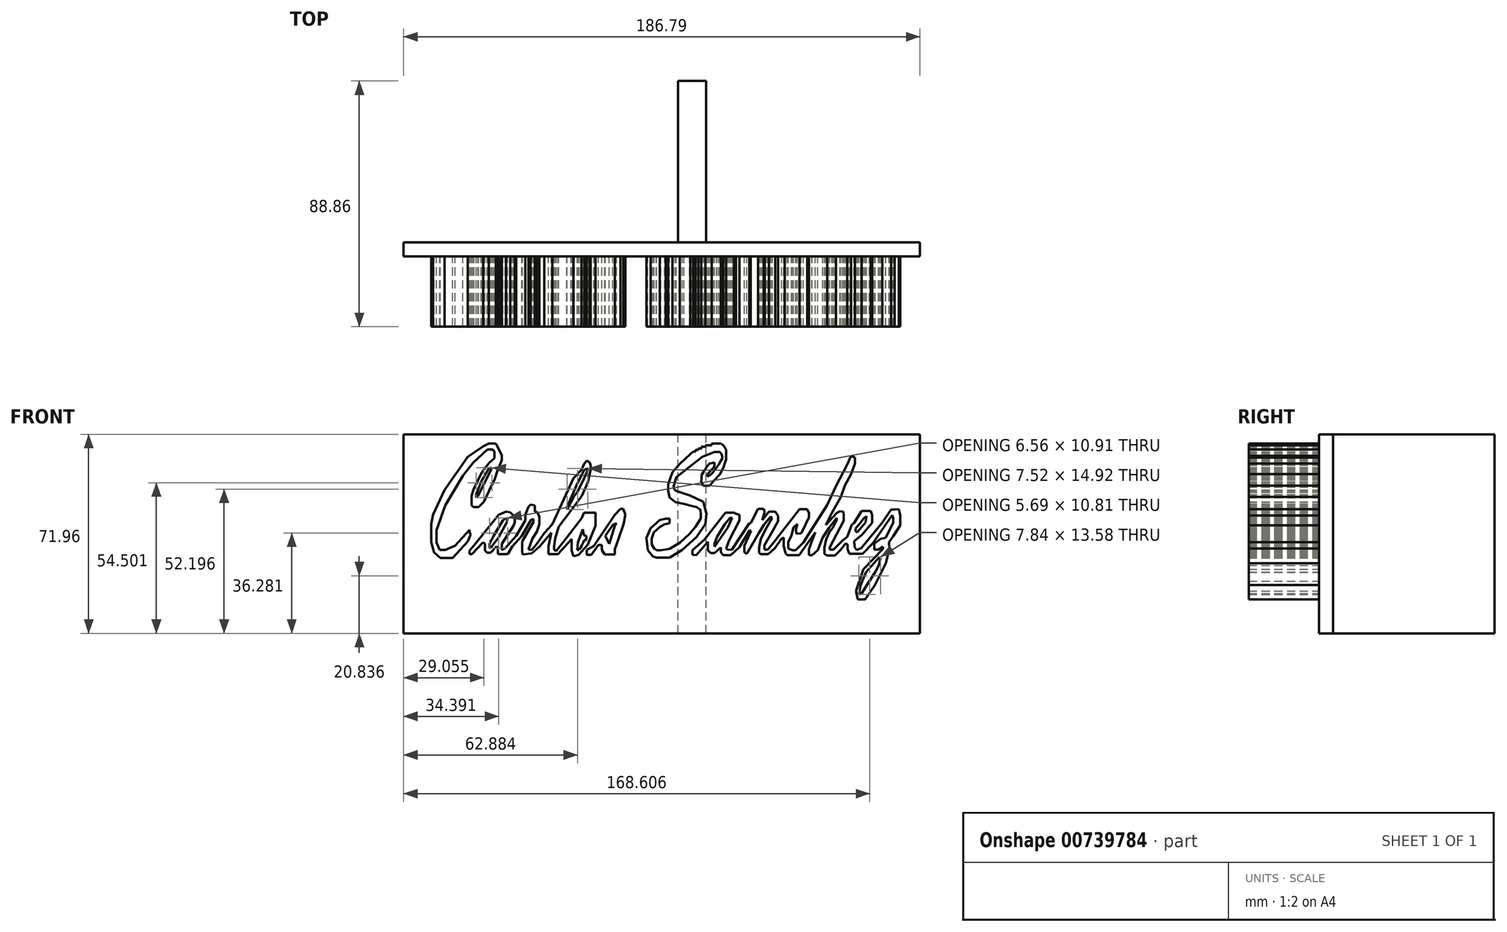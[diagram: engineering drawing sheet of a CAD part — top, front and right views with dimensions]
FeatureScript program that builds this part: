
annotation { "Feature Type Name" : "Feature", "Feature Type Description" : "" }
export const myFeature = defineFeature(function(context is Context, id is Id, definition is map)
    precondition{}
    {
        {
            var Q0;
            Q0=qCreatedBy(makeId("Front.planeOp"),FACE);
            var sketch = newSketch(context, id + "F0", { "sketchPlane" : qUnion([Q0])});
            skLineSegment(sketch, "E0", {"start": v(-63.8, 37.57) * mm, "end": v(-63.8, 39.28) * mm});
            skLineSegment(sketch, "E1", {"start": v(-68.35, 36.5) * mm, "end": v(-71.07, 33.02) * mm});
            skLineSegment(sketch, "E2", {"start": v(-71.07, 33.02) * mm, "end": v(-74.04, 26.76) * mm});
            skLineSegment(sketch, "E3", {"start": v(-74.04, 26.76) * mm, "end": v(-74.73, 24.6) * mm});
            skLineSegment(sketch, "E4", {"start": v(-74.73, 24.6) * mm, "end": v(-74.73, 21.13) * mm});
            skLineSegment(sketch, "E5", {"start": v(-74.73, 21.13) * mm, "end": v(-74.04, 20.56) * mm});
            skLineSegment(sketch, "E6", {"start": v(-74.04, 20.56) * mm, "end": v(-72.2, 20.56) * mm});
            skLineSegment(sketch, "E7", {"start": v(-72.2, 20.56) * mm, "end": v(-70.3, 22.4) * mm});
            skLineSegment(sketch, "E8", {"start": v(-70.3, 22.4) * mm, "end": v(-68.35, 26.44) * mm});
            skLineSegment(sketch, "E9", {"start": v(-68.35, 26.44) * mm, "end": v(-66.39, 30.68) * mm});
            skLineSegment(sketch, "E10", {"start": v(-66.39, 30.68) * mm, "end": v(-65.44, 33.4) * mm});
            skLineSegment(sketch, "E11", {"start": v(-65.44, 33.4) * mm, "end": v(-63.8, 37.57) * mm});
            skPoint(sketch, "E12.startSnap0", {"position": v(-63.8, 38.43) * mm});
            skLineSegment(sketch, "E13", {"start": v(-74.23, 36.5) * mm, "end": v(-75.33, 35.09) * mm});
            skLineSegment(sketch, "E14", {"start": v(-75.33, 35.09) * mm, "end": v(-77.92, 31.77) * mm});
            skLineSegment(sketch, "E15", {"start": v(-77.92, 31.77) * mm, "end": v(-84.22, 21.2) * mm});
            skLineSegment(sketch, "E16", {"start": v(-87.44, 12.09) * mm, "end": v(-87.44, 7.66) * mm});
            skLineSegment(sketch, "E17", {"start": v(-87.44, 7.66) * mm, "end": v(-86.3, 4.94) * mm});
            skLineSegment(sketch, "E18", {"start": v(-86.3, 4.94) * mm, "end": v(-84.22, 4.94) * mm});
            skLineSegment(sketch, "E19", {"start": v(-84.22, 4.94) * mm, "end": v(-80.74, 6.59) * mm});
            skLineSegment(sketch, "E20", {"start": v(-80.74, 6.59) * mm, "end": v(-76.13, 11.65) * mm});
            skLineSegment(sketch, "E21", {"start": v(-76.13, 11.65) * mm, "end": v(-75.53, 12.3) * mm});
            skLineSegment(sketch, "E22", {"start": v(-75.53, 12.3) * mm, "end": v(-75.53, 11.65) * mm});
            skLineSegment(sketch, "E23", {"start": v(-75.53, 11.65) * mm, "end": v(-75.05, 10.45) * mm});
            skLineSegment(sketch, "E24", {"start": v(-75.05, 10.45) * mm, "end": v(-76.13, 8.03) * mm});
            skLineSegment(sketch, "E25", {"start": v(-76.13, 8.03) * mm, "end": v(-78.05, 5.92) * mm});
            skLineSegment(sketch, "E26", {"start": v(-78.05, 5.92) * mm, "end": v(-81.6, 2.02) * mm});
            skLineSegment(sketch, "E27", {"start": v(-81.6, 2.02) * mm, "end": v(-86.05, 2.02) * mm});
            skLineSegment(sketch, "E28", {"start": v(-86.05, 2.02) * mm, "end": v(-88.33, 4.1) * mm});
            skLineSegment(sketch, "E29", {"start": v(-88.33, 4.1) * mm, "end": v(-89.34, 7.85) * mm});
            skLineSegment(sketch, "E30", {"start": v(-89.34, 7.85) * mm, "end": v(-89.34, 14.24) * mm});
            skLineSegment(sketch, "E31", {"start": v(-89.34, 14.24) * mm, "end": v(-88.65, 17.72) * mm});
            skLineSegment(sketch, "E32", {"start": v(-88.65, 17.72) * mm, "end": v(-84.51, 26.72) * mm});
            skLineSegment(sketch, "E33", {"start": v(-84.51, 26.72) * mm, "end": v(-76.13, 38.63) * mm});
            skLineSegment(sketch, "E34", {"start": v(-76.13, 38.63) * mm, "end": v(-70.56, 42.5) * mm});
            skLineSegment(sketch, "E35", {"start": v(-70.56, 42.5) * mm, "end": v(-68.54, 43.52) * mm});
            skLineSegment(sketch, "E36", {"start": v(-68.54, 43.52) * mm, "end": v(-65.94, 43.52) * mm});
            skLineSegment(sketch, "E37", {"start": v(-65.94, 43.52) * mm, "end": v(-65.19, 42.13) * mm});
            skLineSegment(sketch, "E38", {"start": v(-65.19, 42.13) * mm, "end": v(-64.3, 40.23) * mm});
            skLineSegment(sketch, "E39", {"start": v(-64.3, 40.23) * mm, "end": v(-63.8, 39.28) * mm});
            skLineSegment(sketch, "E40", {"start": v(-67.4, 34.6) * mm, "end": v(-72.46, 24.6) * mm});
            skLineSegment(sketch, "E41", {"start": v(-72.46, 24.6) * mm, "end": v(-73.1, 23.92) * mm});
            skLineSegment(sketch, "E42", {"start": v(-73.1, 23.92) * mm, "end": v(-73.1, 25.12) * mm});
            skLineSegment(sketch, "E43", {"start": v(-73.1, 25.12) * mm, "end": v(-71.32, 29.6) * mm});
            skLineSegment(sketch, "E44", {"start": v(-71.32, 29.6) * mm, "end": v(-68.35, 34.73) * mm});
            skLineSegment(sketch, "E45", {"start": v(-68.35, 34.73) * mm, "end": v(-67.4, 34.6) * mm});
            skLineSegment(sketch, "E46", {"start": v(-75.53, 4.75) * mm, "end": v(-73.77, 6.68) * mm});
            skLineSegment(sketch, "E47", {"start": v(-73.77, 6.68) * mm, "end": v(-64.93, 17.72) * mm});
            skLineSegment(sketch, "E48", {"start": v(-64.93, 17.72) * mm, "end": v(-62.21, 18.86) * mm});
            skLineSegment(sketch, "E49", {"start": v(-62.21, 18.86) * mm, "end": v(-60.72, 18.56) * mm});
            skLineSegment(sketch, "E50", {"start": v(-60.72, 18.56) * mm, "end": v(-59.8, 17.72) * mm});
            skLineSegment(sketch, "E51", {"start": v(-59.8, 17.72) * mm, "end": v(-59.08, 17.06) * mm});
            skLineSegment(sketch, "E52", {"start": v(-59.08, 17.06) * mm, "end": v(-59.08, 15.06) * mm});
            skLineSegment(sketch, "E53", {"start": v(-59.08, 15.06) * mm, "end": v(-59.52, 13.93) * mm});
            skLineSegment(sketch, "E54", {"start": v(-59.52, 13.93) * mm, "end": v(-63.8, 7.16) * mm});
            skLineSegment(sketch, "E55", {"start": v(-63.8, 7.16) * mm, "end": v(-63.8, 5) * mm});
            skLineSegment(sketch, "E56", {"start": v(-63.8, 5) * mm, "end": v(-62.53, 5.7) * mm});
            skLineSegment(sketch, "E57", {"start": v(-62.53, 5.7) * mm, "end": v(-58.57, 10.04) * mm});
            skLineSegment(sketch, "E58", {"start": v(-58.57, 10.04) * mm, "end": v(-55.32, 15.7) * mm});
            skLineSegment(sketch, "E59", {"start": v(-55.32, 15.7) * mm, "end": v(-55.32, 17.72) * mm});
            skLineSegment(sketch, "E60", {"start": v(-55.32, 17.72) * mm, "end": v(-54.2, 20.57) * mm});
            skLineSegment(sketch, "E61", {"start": v(-54.2, 20.57) * mm, "end": v(-53.42, 21.42) * mm});
            skLineSegment(sketch, "E62", {"start": v(-53.42, 21.42) * mm, "end": v(-51.84, 21.1) * mm});
            skLineSegment(sketch, "E63", {"start": v(-51.84, 21.1) * mm, "end": v(-51.84, 18.86) * mm});
            skLineSegment(sketch, "E64", {"start": v(-51.84, 18.86) * mm, "end": v(-51, 18.69) * mm});
            skLineSegment(sketch, "E65", {"start": v(-51, 18.69) * mm, "end": v(-50.2, 16.96) * mm});
            skLineSegment(sketch, "E66", {"start": v(-50.2, 16.96) * mm, "end": v(-50.2, 14.3) * mm});
            skLineSegment(sketch, "E67", {"start": v(-50.2, 14.3) * mm, "end": v(-51.13, 11.65) * mm});
            skLineSegment(sketch, "E68", {"start": v(-51.13, 11.65) * mm, "end": v(-52.8, 9.05) * mm});
            skLineSegment(sketch, "E69", {"start": v(-52.8, 9.05) * mm, "end": v(-53.7, 6.44) * mm});
            skLineSegment(sketch, "E70", {"start": v(-53.7, 6.44) * mm, "end": v(-54.14, 5.18) * mm});
            skLineSegment(sketch, "E71", {"start": v(-54.14, 5.18) * mm, "end": v(-53.05, 4.96) * mm});
            skLineSegment(sketch, "E72", {"start": v(-53.05, 4.96) * mm, "end": v(-51.21, 6.98) * mm});
            skLineSegment(sketch, "E73", {"start": v(-51.21, 6.98) * mm, "end": v(-48.37, 11.14) * mm});
            skLineSegment(sketch, "E74", {"start": v(-48.37, 11.14) * mm, "end": v(-45.56, 14.22) * mm});
            skLineSegment(sketch, "E75", {"start": v(-75.53, 4.25) * mm, "end": v(-75.53, 3.43) * mm});
            skLineSegment(sketch, "E76", {"start": v(-75.53, 3.43) * mm, "end": v(-74.54, 3.43) * mm});
            skLineSegment(sketch, "E77", {"start": v(-74.54, 3.43) * mm, "end": v(-70.65, 7.7) * mm});
            skLineSegment(sketch, "E78", {"start": v(-70.65, 7.7) * mm, "end": v(-69.91, 7.26) * mm});
            skLineSegment(sketch, "E79", {"start": v(-69.91, 7.26) * mm, "end": v(-69.91, 4.75) * mm});
            skLineSegment(sketch, "E80", {"start": v(-69.91, 4.75) * mm, "end": v(-69.07, 4) * mm});
            skLineSegment(sketch, "E81", {"start": v(-69.07, 4) * mm, "end": v(-67.84, 4) * mm});
            skLineSegment(sketch, "E82", {"start": v(-67.84, 4) * mm, "end": v(-65.73, 6.3) * mm});
            skLineSegment(sketch, "E83", {"start": v(-65.73, 6.3) * mm, "end": v(-65.2, 5.84) * mm});
            skLineSegment(sketch, "E84", {"start": v(-65.2, 5.84) * mm, "end": v(-65.2, 3.43) * mm});
            skLineSegment(sketch, "E85", {"start": v(-65.2, 3.43) * mm, "end": v(-61.64, 3.43) * mm});
            skLineSegment(sketch, "E86", {"start": v(-61.64, 3.43) * mm, "end": v(-59.99, 6.3) * mm});
            skLineSegment(sketch, "E87", {"start": v(-59.99, 6.3) * mm, "end": v(-56.58, 10.04) * mm});
            skLineSegment(sketch, "E88", {"start": v(-56.58, 10.04) * mm, "end": v(-53.29, 15.77) * mm});
            skLineSegment(sketch, "E89", {"start": v(-53.29, 15.77) * mm, "end": v(-52.54, 16.33) * mm});
            skLineSegment(sketch, "E90", {"start": v(-52.54, 16.33) * mm, "end": v(-52.29, 15.25) * mm});
            skLineSegment(sketch, "E91", {"start": v(-52.29, 15.25) * mm, "end": v(-56.45, 8) * mm});
            skLineSegment(sketch, "E92", {"start": v(-56.45, 8) * mm, "end": v(-56.45, 4.75) * mm});
            skLineSegment(sketch, "E93", {"start": v(-56.45, 4.75) * mm, "end": v(-56.27, 3.3) * mm});
            skLineSegment(sketch, "E94", {"start": v(-56.27, 3.3) * mm, "end": v(-52.97, 3.72) * mm});
            skLineSegment(sketch, "E95", {"start": v(-52.97, 3.72) * mm, "end": v(-50.14, 6.3) * mm});
            skLineSegment(sketch, "E96", {"start": v(-50.14, 6.3) * mm, "end": v(-45.84, 11.27) * mm});
            skLineSegment(sketch, "E97", {"start": v(-45.84, 11.27) * mm, "end": v(-46.91, 6.3) * mm});
            skLineSegment(sketch, "E98", {"start": v(-46.91, 6.3) * mm, "end": v(-46.91, 3.43) * mm});
            skLineSegment(sketch, "E99", {"start": v(-46.91, 3.43) * mm, "end": v(-43.5, 3.43) * mm});
            skLineSegment(sketch, "E100", {"start": v(-43.5, 3.43) * mm, "end": v(-41.15, 6) * mm});
            skLineSegment(sketch, "E101", {"start": v(-41.15, 6) * mm, "end": v(-38.46, 8.95) * mm});
            skLineSegment(sketch, "E102", {"start": v(-38.46, 8.95) * mm, "end": v(-38.46, 4.75) * mm});
            skLineSegment(sketch, "E103", {"start": v(-38.46, 4.75) * mm, "end": v(-37.87, 2.73) * mm});
            skLineSegment(sketch, "E104", {"start": v(-37.87, 2.73) * mm, "end": v(-36.03, 3.27) * mm});
            skLineSegment(sketch, "E105", {"start": v(-36.03, 3.27) * mm, "end": v(-32.66, 6.95) * mm});
            skLineSegment(sketch, "E106", {"start": v(-32.66, 6.95) * mm, "end": v(-29.84, 13.73) * mm});
            skLineSegment(sketch, "E107", {"start": v(-29.84, 13.73) * mm, "end": v(-29.84, 17.9) * mm});
            skLineSegment(sketch, "E108", {"start": v(-45.56, 14.22) * mm, "end": v(-37.87, 30.87) * mm});
            skLineSegment(sketch, "E109", {"start": v(-37.87, 30.87) * mm, "end": v(-35, 34.02) * mm});
            skLineSegment(sketch, "E110", {"start": v(-35, 34.02) * mm, "end": v(-33.95, 36.3) * mm});
            skLineSegment(sketch, "E111", {"start": v(-33.95, 36.3) * mm, "end": v(-33.12, 37.22) * mm});
            skLineSegment(sketch, "E112", {"start": v(-33.12, 37.22) * mm, "end": v(-32.02, 36.72) * mm});
            skLineSegment(sketch, "E113", {"start": v(-32.02, 36.72) * mm, "end": v(-31.67, 35.68) * mm});
            skLineSegment(sketch, "E114", {"start": v(-31.67, 35.68) * mm, "end": v(-31.6, 33.97) * mm});
            skLineSegment(sketch, "E115", {"start": v(-32.66, 29.42) * mm, "end": v(-33.95, 26.59) * mm});
            skLineSegment(sketch, "E116", {"start": v(-33.95, 26.59) * mm, "end": v(-34.88, 24.55) * mm});
            skLineSegment(sketch, "E117", {"start": v(-34.88, 24.55) * mm, "end": v(-38.72, 19.18) * mm});
            skLineSegment(sketch, "E118", {"start": v(-38.72, 19.18) * mm, "end": v(-43.27, 13.36) * mm});
            skLineSegment(sketch, "E119", {"start": v(-43.27, 13.36) * mm, "end": v(-44.47, 9.06) * mm});
            skLineSegment(sketch, "E120", {"start": v(-44.47, 9.06) * mm, "end": v(-44.85, 6.28) * mm});
            skLineSegment(sketch, "E121", {"start": v(-44.85, 6.28) * mm, "end": v(-44.85, 5.01) * mm});
            skLineSegment(sketch, "E122", {"start": v(-44.85, 5.01) * mm, "end": v(-44.1, 4.66) * mm});
            skLineSegment(sketch, "E123", {"start": v(-44.1, 4.66) * mm, "end": v(-40.24, 9.5) * mm});
            skLineSegment(sketch, "E124", {"start": v(-40.24, 9.5) * mm, "end": v(-34.88, 16.58) * mm});
            skLineSegment(sketch, "E125", {"start": v(-34.88, 16.58) * mm, "end": v(-34.02, 18.46) * mm});
            skLineSegment(sketch, "E126", {"start": v(-34.02, 18.46) * mm, "end": v(-31.95, 18.46) * mm});
            skLineSegment(sketch, "E127", {"start": v(-31.95, 18.46) * mm, "end": v(-29.87, 18.46) * mm});
            skLineSegment(sketch, "E128", {"start": v(-29.87, 18.46) * mm, "end": v(-29.84, 17.9) * mm});
            skLineSegment(sketch, "E129", {"start": v(-31, 16.96) * mm, "end": v(-32.04, 15.59) * mm});
            skLineSegment(sketch, "E130", {"start": v(-32.66, 29.42) * mm, "end": v(-31.6, 33.97) * mm});
            skLineSegment(sketch, "E131", {"start": v(-32.66, 33.97) * mm, "end": v(-33.97, 31.09) * mm});
            skLineSegment(sketch, "E132", {"start": v(-40.17, 19.55) * mm, "end": v(-37.45, 24.68) * mm});
            skLineSegment(sketch, "E133", {"start": v(-37.45, 24.68) * mm, "end": v(-36.5, 25.81) * mm});
            skLineSegment(sketch, "E134", {"start": v(-36.5, 25.81) * mm, "end": v(-33.97, 31.09) * mm});
            skLineSegment(sketch, "E135", {"start": v(-40.17, 19.55) * mm, "end": v(-40.17, 20.44) * mm});
            skLineSegment(sketch, "E136", {"start": v(-40.17, 20.44) * mm, "end": v(-36.5, 29.04) * mm});
            skLineSegment(sketch, "E137", {"start": v(-36.5, 29.04) * mm, "end": v(-33.89, 33.97) * mm});
            skLineSegment(sketch, "E138", {"start": v(-33.89, 33.97) * mm, "end": v(-32.66, 34.48) * mm});
            skLineSegment(sketch, "E139", {"start": v(-33.03, 4.95) * mm, "end": v(-30.56, 6.34) * mm});
            skLineSegment(sketch, "E140", {"start": v(-30.56, 6.34) * mm, "end": v(-26.83, 11.84) * mm});
            skLineSegment(sketch, "E141", {"start": v(-26.83, 11.84) * mm, "end": v(-22.85, 17.66) * mm});
            skLineSegment(sketch, "E142", {"start": v(-22.85, 17.66) * mm, "end": v(-20.82, 19.88) * mm});
            skLineSegment(sketch, "E143", {"start": v(-20.82, 19.88) * mm, "end": v(-19.81, 19.88) * mm});
            skLineSegment(sketch, "E144", {"start": v(-19.81, 19.88) * mm, "end": v(-19.05, 17.66) * mm});
            skLineSegment(sketch, "E145", {"start": v(-19.05, 17.66) * mm, "end": v(-19.75, 14.43) * mm});
            skLineSegment(sketch, "E146", {"start": v(-19.75, 14.43) * mm, "end": v(-21.65, 8.8) * mm});
            skLineSegment(sketch, "E147", {"start": v(-21.65, 8.8) * mm, "end": v(-22.85, 5.26) * mm});
            skLineSegment(sketch, "E148", {"start": v(-24.87, 7.22) * mm, "end": v(-22.85, 13.8) * mm});
            skLineSegment(sketch, "E149", {"start": v(-22.85, 13.8) * mm, "end": v(-22.2, 14.7) * mm});
            skLineSegment(sketch, "E150", {"start": v(-22.2, 14.7) * mm, "end": v(-23.6, 13.99) * mm});
            skLineSegment(sketch, "E151", {"start": v(-23.6, 13.99) * mm, "end": v(-26.38, 10.14) * mm});
            skLineSegment(sketch, "E152", {"start": v(-26.38, 10.14) * mm, "end": v(-24.87, 7.22) * mm});
            skLineSegment(sketch, "E153", {"start": v(-33.03, 4.95) * mm, "end": v(-33.03, 3.24) * mm});
            skLineSegment(sketch, "E154", {"start": v(-33.03, 3.24) * mm, "end": v(-31.38, 3.24) * mm});
            skLineSegment(sketch, "E155", {"start": v(-31.38, 3.24) * mm, "end": v(-28.85, 6.77) * mm});
            skLineSegment(sketch, "E156", {"start": v(-28.85, 6.77) * mm, "end": v(-27.65, 6.77) * mm});
            skLineSegment(sketch, "E157", {"start": v(-27.65, 6.77) * mm, "end": v(-27.65, 4.95) * mm});
            skLineSegment(sketch, "E158", {"start": v(-27.65, 4.95) * mm, "end": v(-26.64, 3.37) * mm});
            skLineSegment(sketch, "E159", {"start": v(-26.64, 3.37) * mm, "end": v(-22.85, 3.37) * mm});
            skLineSegment(sketch, "E160", {"start": v(-22.85, 3.37) * mm, "end": v(-22.85, 5.26) * mm});
            skLineSegment(sketch, "E161", {"start": v(-9.13, 2.67) * mm, "end": v(-7.93, 2.27) * mm});
            skLineSegment(sketch, "E162", {"start": v(-7.93, 2.27) * mm, "end": v(-3.06, 2.27) * mm});
            skLineSegment(sketch, "E163", {"start": v(-3.06, 2.27) * mm, "end": v(1.43, 4.95) * mm});
            skLineSegment(sketch, "E164", {"start": v(1.43, 4.95) * mm, "end": v(6.75, 9.7) * mm});
            skLineSegment(sketch, "E165", {"start": v(9.09, 22.46) * mm, "end": v(4.34, 24.68) * mm});
            skLineSegment(sketch, "E166", {"start": v(4.34, 24.68) * mm, "end": v(-1.06, 26.5) * mm});
            skLineSegment(sketch, "E167", {"start": v(-3.53, 28.7) * mm, "end": v(-3.53, 26.32) * mm});
            skLineSegment(sketch, "E168", {"start": v(-3.53, 26.32) * mm, "end": v(-3.06, 23.92) * mm});
            skLineSegment(sketch, "E169", {"start": v(-3.06, 23.92) * mm, "end": v(-0.9, 22.34) * mm});
            skLineSegment(sketch, "E170", {"start": v(-0.9, 22.34) * mm, "end": v(2.07, 21.64) * mm});
            skLineSegment(sketch, "E171", {"start": v(2.07, 21.64) * mm, "end": v(5.1, 20.82) * mm});
            skLineSegment(sketch, "E172", {"start": v(5.1, 20.82) * mm, "end": v(6.75, 20.44) * mm});
            skLineSegment(sketch, "E173", {"start": v(6.75, 20.44) * mm, "end": v(8.07, 19.5) * mm});
            skLineSegment(sketch, "E174", {"start": v(8.2, 17.66) * mm, "end": v(8.2, 16.4) * mm});
            skLineSegment(sketch, "E175", {"start": v(8.2, 16.4) * mm, "end": v(6.37, 13.36) * mm});
            skLineSegment(sketch, "E176", {"start": v(6.37, 13.36) * mm, "end": v(4.22, 10.83) * mm});
            skLineSegment(sketch, "E177", {"start": v(0.68, 7.73) * mm, "end": v(-3.06, 5.4) * mm});
            skLineSegment(sketch, "E178", {"start": v(-3.06, 5.4) * mm, "end": v(-6.28, 4.88) * mm});
            skLineSegment(sketch, "E179", {"start": v(-6.28, 4.88) * mm, "end": v(-7.73, 4.88) * mm});
            skLineSegment(sketch, "E180", {"start": v(5.23, 4.88) * mm, "end": v(9.5, 8.7) * mm});
            skLineSegment(sketch, "E181", {"start": v(9.5, 8.7) * mm, "end": v(17.12, 18.42) * mm});
            skLineSegment(sketch, "E182", {"start": v(17.12, 18.42) * mm, "end": v(20.15, 18.42) * mm});
            skLineSegment(sketch, "E183", {"start": v(20.15, 18.42) * mm, "end": v(20.91, 18.04) * mm});
            skLineSegment(sketch, "E184", {"start": v(20.91, 18.04) * mm, "end": v(22.19, 17.76) * mm});
            skLineSegment(sketch, "E185", {"start": v(5.23, 4.88) * mm, "end": v(5.23, 3.18) * mm});
            skLineSegment(sketch, "E186", {"start": v(5.23, 3.18) * mm, "end": v(6.56, 3.11) * mm});
            skLineSegment(sketch, "E187", {"start": v(6.56, 3.11) * mm, "end": v(10.8, 7.92) * mm});
            skLineSegment(sketch, "E188", {"start": v(10.8, 7.92) * mm, "end": v(10.8, 4.88) * mm});
            skLineSegment(sketch, "E189", {"start": v(10.8, 4.88) * mm, "end": v(11.74, 3.82) * mm});
            skLineSegment(sketch, "E190", {"start": v(11.74, 3.82) * mm, "end": v(13.2, 3.87) * mm});
            skLineSegment(sketch, "E191", {"start": v(13.2, 3.87) * mm, "end": v(15.42, 5.86) * mm});
            skLineSegment(sketch, "E192", {"start": v(15.42, 5.86) * mm, "end": v(15.42, 4.13) * mm});
            skLineSegment(sketch, "E193", {"start": v(15.42, 4.13) * mm, "end": v(16.32, 3.11) * mm});
            skLineSegment(sketch, "E194", {"start": v(16.32, 3.11) * mm, "end": v(19.01, 3.11) * mm});
            skLineSegment(sketch, "E195", {"start": v(19.01, 3.11) * mm, "end": v(22.25, 6) * mm});
            skLineSegment(sketch, "E196", {"start": v(22.25, 6) * mm, "end": v(25.84, 12.16) * mm});
            skLineSegment(sketch, "E197", {"start": v(25.84, 12.16) * mm, "end": v(26.32, 11.88) * mm});
            skLineSegment(sketch, "E198", {"start": v(26.32, 11.88) * mm, "end": v(25.2, 9.37) * mm});
            skLineSegment(sketch, "E199", {"start": v(25.2, 9.37) * mm, "end": v(23.95, 6.6) * mm});
            skLineSegment(sketch, "E200", {"start": v(23.95, 6.6) * mm, "end": v(23.95, 4.06) * mm});
            skLineSegment(sketch, "E201", {"start": v(23.95, 4.06) * mm, "end": v(24.83, 3.62) * mm});
            skLineSegment(sketch, "E202", {"start": v(24.83, 3.62) * mm, "end": v(29.13, 11.14) * mm});
            skLineSegment(sketch, "E203", {"start": v(29.13, 11.14) * mm, "end": v(31.1, 14.18) * mm});
            skLineSegment(sketch, "E204", {"start": v(31.1, 14.18) * mm, "end": v(33.43, 17.09) * mm});
            skLineSegment(sketch, "E205", {"start": v(33.43, 17.09) * mm, "end": v(34.04, 16.6) * mm});
            skLineSegment(sketch, "E206", {"start": v(34.04, 16.6) * mm, "end": v(31.91, 12.98) * mm});
            skLineSegment(sketch, "E207", {"start": v(31.91, 12.98) * mm, "end": v(29.89, 9.12) * mm});
            skLineSegment(sketch, "E208", {"start": v(29.89, 9.12) * mm, "end": v(29.32, 5.9) * mm});
            skLineSegment(sketch, "E209", {"start": v(29.32, 5.9) * mm, "end": v(29.32, 3.94) * mm});
            skLineSegment(sketch, "E210", {"start": v(29.32, 3.94) * mm, "end": v(29.76, 3.43) * mm});
            skLineSegment(sketch, "E211", {"start": v(29.76, 3.43) * mm, "end": v(32.55, 3.43) * mm});
            skLineSegment(sketch, "E212", {"start": v(32.55, 3.43) * mm, "end": v(35, 5.62) * mm});
            skLineSegment(sketch, "E213", {"start": v(35, 5.62) * mm, "end": v(37.48, 9.12) * mm});
            skLineSegment(sketch, "E214", {"start": v(37.48, 9.12) * mm, "end": v(38.24, 9.5) * mm});
            skLineSegment(sketch, "E215", {"start": v(38.24, 9.5) * mm, "end": v(38.24, 6.6) * mm});
            skLineSegment(sketch, "E216", {"start": v(38.24, 6.6) * mm, "end": v(38.87, 3.8) * mm});
            skLineSegment(sketch, "E217", {"start": v(38.87, 3.8) * mm, "end": v(39.49, 3.11) * mm});
            skLineSegment(sketch, "E218", {"start": v(39.49, 3.11) * mm, "end": v(43.8, 3.11) * mm});
            skLineSegment(sketch, "E219", {"start": v(43.8, 3.11) * mm, "end": v(48.3, 9.63) * mm});
            skLineSegment(sketch, "E220", {"start": v(48.3, 9.63) * mm, "end": v(49.68, 11.33) * mm});
            skLineSegment(sketch, "E221", {"start": v(49.68, 11.33) * mm, "end": v(48.42, 8.49) * mm});
            skLineSegment(sketch, "E222", {"start": v(48.42, 8.49) * mm, "end": v(47.28, 5.2) * mm});
            skLineSegment(sketch, "E223", {"start": v(47.28, 5.2) * mm, "end": v(47.28, 3.11) * mm});
            skLineSegment(sketch, "E224", {"start": v(47.28, 3.11) * mm, "end": v(48.48, 3.11) * mm});
            skLineSegment(sketch, "E225", {"start": v(48.48, 3.11) * mm, "end": v(50.46, 4.88) * mm});
            skLineSegment(sketch, "E226", {"start": v(50.46, 4.88) * mm, "end": v(52.27, 9.5) * mm});
            skLineSegment(sketch, "E227", {"start": v(52.27, 9.5) * mm, "end": v(54.74, 13.1) * mm});
            skLineSegment(sketch, "E228", {"start": v(54.74, 13.1) * mm, "end": v(57.4, 16.58) * mm});
            skLineSegment(sketch, "E229", {"start": v(57.4, 16.58) * mm, "end": v(57.4, 15.76) * mm});
            skLineSegment(sketch, "E230", {"start": v(57.4, 15.76) * mm, "end": v(55.94, 13.04) * mm});
            skLineSegment(sketch, "E231", {"start": v(55.94, 13.04) * mm, "end": v(54.81, 11.56) * mm});
            skLineSegment(sketch, "E232", {"start": v(54.81, 11.56) * mm, "end": v(53.54, 8.87) * mm});
            skLineSegment(sketch, "E233", {"start": v(53.54, 8.87) * mm, "end": v(52.97, 5.9) * mm});
            skLineSegment(sketch, "E234", {"start": v(52.97, 5.9) * mm, "end": v(52.97, 3.62) * mm});
            skLineSegment(sketch, "E235", {"start": v(52.97, 3.62) * mm, "end": v(53.81, 2.98) * mm});
            skLineSegment(sketch, "E236", {"start": v(53.81, 2.98) * mm, "end": v(56.7, 2.98) * mm});
            skLineSegment(sketch, "E237", {"start": v(56.7, 2.98) * mm, "end": v(58.79, 4.95) * mm});
            skLineSegment(sketch, "E238", {"start": v(58.79, 4.95) * mm, "end": v(60.66, 7.4) * mm});
            skLineSegment(sketch, "E239", {"start": v(22.19, 17.76) * mm, "end": v(22.19, 15.63) * mm});
            skPoint(sketch, "E239.endSnap0", {"position": v(32.26, 15.63) * mm});
            skLineSegment(sketch, "E240", {"start": v(22.19, 15.63) * mm, "end": v(20.66, 12.72) * mm});
            skLineSegment(sketch, "E241", {"start": v(20.66, 12.72) * mm, "end": v(18.38, 8.37) * mm});
            skLineSegment(sketch, "E242", {"start": v(18.38, 8.37) * mm, "end": v(17.3, 5.33) * mm});
            skLineSegment(sketch, "E243", {"start": v(17.3, 5.33) * mm, "end": v(17.8, 5.15) * mm});
            skLineSegment(sketch, "E244", {"start": v(17.8, 5.15) * mm, "end": v(19.46, 5.01) * mm});
            skLineSegment(sketch, "E245", {"start": v(19.46, 5.01) * mm, "end": v(25.78, 14.62) * mm});
            skLineSegment(sketch, "E246", {"start": v(25.78, 14.62) * mm, "end": v(26.22, 14.62) * mm});
            skLineSegment(sketch, "E247", {"start": v(26.22, 14.62) * mm, "end": v(28.98, 19.88) * mm});
            skLineSegment(sketch, "E248", {"start": v(28.98, 19.88) * mm, "end": v(30.96, 19.88) * mm});
            skLineSegment(sketch, "E249", {"start": v(30.96, 19.88) * mm, "end": v(31.34, 18.67) * mm});
            skLineSegment(sketch, "E250", {"start": v(31.34, 18.67) * mm, "end": v(30.46, 15.76) * mm});
            skLineSegment(sketch, "E251", {"start": v(30.46, 15.76) * mm, "end": v(32.92, 18.82) * mm});
            skLineSegment(sketch, "E252", {"start": v(32.92, 18.82) * mm, "end": v(35.14, 18.82) * mm});
            skLineSegment(sketch, "E253", {"start": v(35.14, 18.82) * mm, "end": v(36.21, 17.34) * mm});
            skLineSegment(sketch, "E254", {"start": v(36.21, 17.34) * mm, "end": v(36.21, 15.38) * mm});
            skLineSegment(sketch, "E255", {"start": v(36.21, 15.38) * mm, "end": v(34.06, 11.71) * mm});
            skLineSegment(sketch, "E256", {"start": v(34.06, 11.71) * mm, "end": v(31.22, 6.72) * mm});
            skLineSegment(sketch, "E257", {"start": v(31.22, 6.72) * mm, "end": v(31.22, 5.07) * mm});
            skLineSegment(sketch, "E258", {"start": v(31.22, 5.07) * mm, "end": v(32.42, 5.07) * mm});
            skLineSegment(sketch, "E259", {"start": v(32.42, 5.07) * mm, "end": v(35.14, 8.49) * mm});
            skLineSegment(sketch, "E260", {"start": v(35.14, 8.49) * mm, "end": v(38.62, 12.92) * mm});
            skLineSegment(sketch, "E261", {"start": v(38.62, 12.92) * mm, "end": v(43.86, 19.74) * mm});
            skLineSegment(sketch, "E262", {"start": v(43.86, 19.74) * mm, "end": v(46.65, 19.74) * mm});
            skLineSegment(sketch, "E263", {"start": v(46.65, 19.74) * mm, "end": v(47.28, 18.35) * mm});
            skLineSegment(sketch, "E264", {"start": v(47.28, 18.35) * mm, "end": v(47.28, 16.77) * mm});
            skLineSegment(sketch, "E265", {"start": v(47.28, 16.77) * mm, "end": v(46.14, 14.37) * mm});
            skLineSegment(sketch, "E266", {"start": v(46.14, 14.37) * mm, "end": v(44.5, 10.95) * mm});
            skLineSegment(sketch, "E267", {"start": v(44.5, 10.95) * mm, "end": v(42.73, 10.83) * mm});
            skLineSegment(sketch, "E268", {"start": v(42.73, 10.83) * mm, "end": v(42.6, 12.5) * mm});
            skLineSegment(sketch, "E269", {"start": v(42.6, 12.5) * mm, "end": v(43.17, 14.43) * mm});
            skLineSegment(sketch, "E270", {"start": v(43.17, 14.43) * mm, "end": v(41.71, 13.17) * mm});
            skLineSegment(sketch, "E271", {"start": v(41.71, 13.17) * mm, "end": v(40.96, 10.2) * mm});
            skLineSegment(sketch, "E272", {"start": v(40.96, 10.2) * mm, "end": v(39.82, 7.86) * mm});
            skLineSegment(sketch, "E273", {"start": v(39.82, 7.86) * mm, "end": v(39.82, 5.45) * mm});
            skLineSegment(sketch, "E274", {"start": v(39.82, 5.45) * mm, "end": v(41.4, 4.88) * mm});
            skLineSegment(sketch, "E275", {"start": v(41.4, 4.88) * mm, "end": v(42.47, 4.88) * mm});
            skLineSegment(sketch, "E276", {"start": v(42.47, 4.88) * mm, "end": v(45.25, 7.73) * mm});
            skLineSegment(sketch, "E277", {"start": v(45.25, 7.73) * mm, "end": v(48.54, 12.85) * mm});
            skLineSegment(sketch, "E278", {"start": v(48.54, 12.85) * mm, "end": v(53.98, 21.2) * mm});
            skLineSegment(sketch, "E279", {"start": v(53.98, 21.2) * mm, "end": v(57.14, 28.1) * mm});
            skLineSegment(sketch, "E280", {"start": v(57.14, 28.1) * mm, "end": v(61.19, 35.87) * mm});
            skLineSegment(sketch, "E281", {"start": v(61.19, 35.87) * mm, "end": v(62.52, 39.03) * mm});
            skLineSegment(sketch, "E282", {"start": v(62.52, 39.03) * mm, "end": v(64, 38.4) * mm});
            skLineSegment(sketch, "E283", {"start": v(64, 38.4) * mm, "end": v(64, 36.18) * mm});
            skLineSegment(sketch, "E284", {"start": v(64, 36.18) * mm, "end": v(62.52, 32.4) * mm});
            skLineSegment(sketch, "E285", {"start": v(62.52, 32.4) * mm, "end": v(60.3, 28.28) * mm});
            skLineSegment(sketch, "E286", {"start": v(60.3, 28.28) * mm, "end": v(58.85, 24.23) * mm});
            skLineSegment(sketch, "E287", {"start": v(58.85, 24.23) * mm, "end": v(55.56, 18.29) * mm});
            skLineSegment(sketch, "E288", {"start": v(55.56, 18.29) * mm, "end": v(53.41, 13.99) * mm});
            skLineSegment(sketch, "E289", {"start": v(53.41, 13.99) * mm, "end": v(57.4, 18.29) * mm});
            skLineSegment(sketch, "E290", {"start": v(57.4, 18.29) * mm, "end": v(58.53, 18.99) * mm});
            skLineSegment(sketch, "E291", {"start": v(58.53, 18.99) * mm, "end": v(59.74, 18.86) * mm});
            skLineSegment(sketch, "E292", {"start": v(59.74, 18.86) * mm, "end": v(59.92, 17.6) * mm});
            skLineSegment(sketch, "E293", {"start": v(59.92, 17.6) * mm, "end": v(59.92, 15.57) * mm});
            skLineSegment(sketch, "E294", {"start": v(59.92, 15.57) * mm, "end": v(54.87, 5.9) * mm});
            skLineSegment(sketch, "E295", {"start": v(54.87, 5.9) * mm, "end": v(54.87, 5.07) * mm});
            skLineSegment(sketch, "E296", {"start": v(54.87, 5.07) * mm, "end": v(56.26, 5.07) * mm});
            skLineSegment(sketch, "E297", {"start": v(56.26, 5.07) * mm, "end": v(59.55, 8.43) * mm});
            skLineSegment(sketch, "E298", {"start": v(59.55, 8.43) * mm, "end": v(61.13, 9.75) * mm});
            skLineSegment(sketch, "E299", {"start": v(61.13, 9.75) * mm, "end": v(62.83, 14.18) * mm});
            skLineSegment(sketch, "E300", {"start": v(62.83, 14.18) * mm, "end": v(63.53, 14.69) * mm});
            skLineSegment(sketch, "E301", {"start": v(63.53, 14.69) * mm, "end": v(66.38, 19.06) * mm});
            skLineSegment(sketch, "E302", {"start": v(66.38, 19.06) * mm, "end": v(67.96, 19.06) * mm});
            skLineSegment(sketch, "E303", {"start": v(67.96, 19.06) * mm, "end": v(69.73, 19.06) * mm});
            skLineSegment(sketch, "E304", {"start": v(60.66, 7.4) * mm, "end": v(61.28, 6.93) * mm});
            skLineSegment(sketch, "E305", {"start": v(61.28, 6.93) * mm, "end": v(61.25, 5.2) * mm});
            skLineSegment(sketch, "E306", {"start": v(61.25, 5.2) * mm, "end": v(61.95, 3.56) * mm});
            skLineSegment(sketch, "E307", {"start": v(61.95, 3.56) * mm, "end": v(64.1, 3.56) * mm});
            skLineSegment(sketch, "E308", {"start": v(64.1, 3.56) * mm, "end": v(66.75, 3.56) * mm});
            skLineSegment(sketch, "E309", {"start": v(66.75, 3.56) * mm, "end": v(70.48, 7.4) * mm});
            skLineSegment(sketch, "E310", {"start": v(70.48, 7.4) * mm, "end": v(77.44, 17.53) * mm});
            skLineSegment(sketch, "E311", {"start": v(69.73, 19.06) * mm, "end": v(70.23, 17.6) * mm});
            skLineSegment(sketch, "E312", {"start": v(70.23, 17.6) * mm, "end": v(70.23, 14.75) * mm});
            skLineSegment(sketch, "E313", {"start": v(70.23, 14.75) * mm, "end": v(66.56, 10.45) * mm});
            skLineSegment(sketch, "E314", {"start": v(66.56, 10.45) * mm, "end": v(63.72, 8.17) * mm});
            skLineSegment(sketch, "E315", {"start": v(63.72, 8.17) * mm, "end": v(63.78, 5.96) * mm});
            skLineSegment(sketch, "E316", {"start": v(63.78, 5.96) * mm, "end": v(64.67, 4.95) * mm});
            skLineSegment(sketch, "E317", {"start": v(64.67, 4.95) * mm, "end": v(66.31, 5.64) * mm});
            skLineSegment(sketch, "E318", {"start": v(66.31, 5.64) * mm, "end": v(73.84, 14.94) * mm});
            skLineSegment(sketch, "E319", {"start": v(73.84, 14.94) * mm, "end": v(77.02, 19.58) * mm});
            skLineSegment(sketch, "E320", {"start": v(77.02, 19.58) * mm, "end": v(78.33, 19.58) * mm});
            skLineSegment(sketch, "E321", {"start": v(78.33, 19.58) * mm, "end": v(79.9, 19.68) * mm});
            skLineSegment(sketch, "E322", {"start": v(79.9, 19.68) * mm, "end": v(80.41, 17.47) * mm});
            skLineSegment(sketch, "E323", {"start": v(80.41, 17.47) * mm, "end": v(80.41, 13.86) * mm});
            skLineSegment(sketch, "E324", {"start": v(80.41, 13.86) * mm, "end": v(77.82, 10) * mm});
            skLineSegment(sketch, "E325", {"start": v(77.82, 10) * mm, "end": v(76.34, 7.85) * mm});
            skLineSegment(sketch, "E326", {"start": v(76.34, 7.85) * mm, "end": v(76.4, 5.45) * mm});
            skLineSegment(sketch, "E327", {"start": v(76.4, 5.45) * mm, "end": v(75.16, 0.2) * mm});
            skLineSegment(sketch, "E328", {"start": v(75.16, 0.2) * mm, "end": v(71.18, -7.64) * mm});
            skLineSegment(sketch, "E329", {"start": v(71.18, -7.64) * mm, "end": v(68.7, -11.32) * mm});
            skLineSegment(sketch, "E330", {"start": v(68.7, -11.32) * mm, "end": v(67.65, -12.9) * mm});
            skLineSegment(sketch, "E331", {"start": v(67.65, -12.9) * mm, "end": v(65.05, -12.9) * mm});
            skLineSegment(sketch, "E332", {"start": v(65.05, -12.9) * mm, "end": v(64.35, -9.91) * mm});
            skLineSegment(sketch, "E333", {"start": v(64.35, -9.91) * mm, "end": v(67.07, -1.94) * mm});
            skLineSegment(sketch, "E334", {"start": v(67.07, -1.94) * mm, "end": v(74.15, 5.33) * mm});
            skLineSegment(sketch, "E335", {"start": v(74.15, 5.33) * mm, "end": v(74.15, 6.15) * mm});
            skLineSegment(sketch, "E336", {"start": v(74.15, 6.15) * mm, "end": v(72.5, 5.14) * mm});
            skLineSegment(sketch, "E337", {"start": v(72.5, 5.14) * mm, "end": v(70.93, 5.14) * mm});
            skLineSegment(sketch, "E338", {"start": v(70.93, 5.14) * mm, "end": v(70.93, 7.35) * mm});
            skLineSegment(sketch, "E339", {"start": v(70.93, 7.35) * mm, "end": v(73.4, 9.12) * mm});
            skLineSegment(sketch, "E340", {"start": v(73.4, 9.12) * mm, "end": v(75.04, 9.37) * mm});
            skLineSegment(sketch, "E341", {"start": v(75.04, 9.37) * mm, "end": v(77.77, 14.84) * mm});
            skLineSegment(sketch, "E342", {"start": v(77.77, 14.84) * mm, "end": v(77.77, 16.46) * mm});
            skLineSegment(sketch, "E343", {"start": v(77.77, 16.46) * mm, "end": v(77.44, 17.53) * mm});
            skLineSegment(sketch, "E344", {"start": v(13.2, 6.15) * mm, "end": v(17.94, 13.1) * mm});
            skLineSegment(sketch, "E345", {"start": v(17.94, 13.1) * mm, "end": v(19.52, 16.52) * mm});
            skLineSegment(sketch, "E346", {"start": v(19.52, 16.52) * mm, "end": v(18.89, 16.7) * mm});
            skLineSegment(sketch, "E347", {"start": v(18.89, 16.7) * mm, "end": v(16.8, 14.3) * mm});
            skLineSegment(sketch, "E348", {"start": v(16.8, 14.3) * mm, "end": v(14.02, 9.7) * mm});
            skLineSegment(sketch, "E349", {"start": v(14.02, 9.7) * mm, "end": v(13.2, 7.28) * mm});
            skLineSegment(sketch, "E350", {"start": v(13.2, 7.28) * mm, "end": v(13.2, 6.15) * mm});
            skLineSegment(sketch, "E351", {"start": v(-87.44, 12.09) * mm, "end": v(-84.22, 21.2) * mm});
            skLineSegment(sketch, "E352", {"start": v(-75.53, 4.25) * mm, "end": v(-75.53, 4.75) * mm});
            skLineSegment(sketch, "E353", {"start": v(-67.83, 5.65) * mm, "end": v(-64.99, 9.61) * mm});
            skLineSegment(sketch, "E354", {"start": v(-64.99, 9.61) * mm, "end": v(-61.98, 14.85) * mm});
            skLineSegment(sketch, "E355", {"start": v(-61.98, 14.85) * mm, "end": v(-61.63, 16.43) * mm});
            skLineSegment(sketch, "E356", {"start": v(-61.63, 16.43) * mm, "end": v(-62.18, 16.56) * mm});
            skLineSegment(sketch, "E357", {"start": v(-62.18, 16.56) * mm, "end": v(-63.36, 15.67) * mm});
            skLineSegment(sketch, "E358", {"start": v(-63.36, 15.67) * mm, "end": v(-65.34, 12.51) * mm});
            skLineSegment(sketch, "E359", {"start": v(-65.34, 12.51) * mm, "end": v(-66.82, 9.92) * mm});
            skLineSegment(sketch, "E360", {"start": v(-66.82, 9.92) * mm, "end": v(-68.2, 7.12) * mm});
            skLineSegment(sketch, "E361", {"start": v(-68.2, 7.12) * mm, "end": v(-68.2, 5.8) * mm});
            skLineSegment(sketch, "E362", {"start": v(-68.2, 5.8) * mm, "end": v(-67.83, 5.65) * mm});
            skLineSegment(sketch, "E363", {"start": v(-74.23, 36.5) * mm, "end": v(-68.95, 41.28) * mm});
            skLineSegment(sketch, "E364", {"start": v(-68.95, 41.28) * mm, "end": v(-66.97, 41.28) * mm});
            skLineSegment(sketch, "E365", {"start": v(-66.97, 41.28) * mm, "end": v(-66.46, 40.46) * mm});
            skLineSegment(sketch, "E366", {"start": v(-66.46, 40.46) * mm, "end": v(-66.46, 38.2) * mm});
            skLineSegment(sketch, "E367", {"start": v(-66.46, 38.2) * mm, "end": v(-68.35, 36.5) * mm});
            skLineSegment(sketch, "E368", {"start": v(0.68, 7.73) * mm, "end": v(4.22, 10.83) * mm});
            skLineSegment(sketch, "E369", {"start": v(6.75, 9.7) * mm, "end": v(9.9, 14.35) * mm});
            skLineSegment(sketch, "E370", {"start": v(-9.13, 2.67) * mm, "end": v(-10.98, 4.88) * mm});
            skPoint(sketch, "E370.endSnap0", {"position": v(-7, 4.88) * mm});
            skLineSegment(sketch, "E371", {"start": v(-10.98, 4.88) * mm, "end": v(-11.52, 9.3) * mm});
            skLineSegment(sketch, "E372", {"start": v(-11.52, 9.3) * mm, "end": v(-9.97, 12.87) * mm});
            skLineSegment(sketch, "E373", {"start": v(-9.97, 12.87) * mm, "end": v(-6.66, 15.78) * mm});
            skLineSegment(sketch, "E374", {"start": v(-6.66, 15.78) * mm, "end": v(-4.5, 16.36) * mm});
            skLineSegment(sketch, "E375", {"start": v(-4.5, 16.36) * mm, "end": v(-3.1, 16.36) * mm});
            skLineSegment(sketch, "E376", {"start": v(-3.1, 16.36) * mm, "end": v(-3.1, 14.7) * mm});
            skLineSegment(sketch, "E377", {"start": v(-3.1, 14.7) * mm, "end": v(-4.9, 14.27) * mm});
            skLineSegment(sketch, "E378", {"start": v(-4.9, 14.27) * mm, "end": v(-6.56, 13.44) * mm});
            skLineSegment(sketch, "E379", {"start": v(-6.56, 13.44) * mm, "end": v(-8.75, 11.36) * mm});
            skLineSegment(sketch, "E380", {"start": v(-8.75, 11.36) * mm, "end": v(-9.54, 9.06) * mm});
            skLineSegment(sketch, "E381", {"start": v(-9.54, 9.06) * mm, "end": v(-9.54, 7.08) * mm});
            skLineSegment(sketch, "E382", {"start": v(-9.54, 7.08) * mm, "end": v(-8.71, 5.53) * mm});
            skLineSegment(sketch, "E383", {"start": v(-8.71, 5.53) * mm, "end": v(-7.73, 4.88) * mm});
            skLineSegment(sketch, "E384", {"start": v(8.2, 17.66) * mm, "end": v(8.07, 19.5) * mm});
            skLineSegment(sketch, "E385", {"start": v(9.9, 14.35) * mm, "end": v(10.24, 18.09) * mm});
            skLineSegment(sketch, "E386", {"start": v(10.24, 18.09) * mm, "end": v(9.09, 22.46) * mm});
            skLineSegment(sketch, "E387", {"start": v(-1.06, 26.5) * mm, "end": v(-1.66, 27.76) * mm});
            skLineSegment(sketch, "E388", {"start": v(-1.66, 27.76) * mm, "end": v(-0.7, 31.32) * mm});
            skLineSegment(sketch, "E389", {"start": v(-0.7, 31.32) * mm, "end": v(8.7, 38.7) * mm});
            skLineSegment(sketch, "E390", {"start": v(8.7, 38.7) * mm, "end": v(13.16, 40.43) * mm});
            skLineSegment(sketch, "E391", {"start": v(13.16, 40.43) * mm, "end": v(15.14, 40.5) * mm});
            skLineSegment(sketch, "E392", {"start": v(15.14, 40.5) * mm, "end": v(15.75, 39.63) * mm});
            skLineSegment(sketch, "E393", {"start": v(15.75, 39.63) * mm, "end": v(16.07, 38.34) * mm});
            skLineSegment(sketch, "E394", {"start": v(16.07, 38.34) * mm, "end": v(15.42, 37.26) * mm});
            skLineSegment(sketch, "E395", {"start": v(15.42, 37.26) * mm, "end": v(14.7, 35.93) * mm});
            skLineSegment(sketch, "E396", {"start": v(14.7, 35.93) * mm, "end": v(13.95, 34.81) * mm});
            skLineSegment(sketch, "E397", {"start": v(13.95, 34.81) * mm, "end": v(12.37, 32.84) * mm});
            skLineSegment(sketch, "E398", {"start": v(12.37, 32.84) * mm, "end": v(11.47, 32.04) * mm});
            skLineSegment(sketch, "E399", {"start": v(11.47, 32.04) * mm, "end": v(10.68, 31.54) * mm});
            skLineSegment(sketch, "E400", {"start": v(10.68, 31.54) * mm, "end": v(10.6, 32.48) * mm});
            skLineSegment(sketch, "E401", {"start": v(10.6, 32.48) * mm, "end": v(12.9, 34.81) * mm});
            skLineSegment(sketch, "E402", {"start": v(12.9, 34.81) * mm, "end": v(13.23, 35.78) * mm});
            skLineSegment(sketch, "E403", {"start": v(13.23, 35.78) * mm, "end": v(13.23, 36.58) * mm});
            skLineSegment(sketch, "E404", {"start": v(13.23, 36.58) * mm, "end": v(11.36, 36.22) * mm});
            skLineSegment(sketch, "E405", {"start": v(11.36, 36.22) * mm, "end": v(10.93, 35.75) * mm});
            skLineSegment(sketch, "E406", {"start": v(10.93, 35.75) * mm, "end": v(10.28, 34.81) * mm});
            skLineSegment(sketch, "E407", {"start": v(10.28, 34.81) * mm, "end": v(9.2, 33.27) * mm});
            skLineSegment(sketch, "E408", {"start": v(9.2, 33.27) * mm, "end": v(8.48, 32.08) * mm});
            skLineSegment(sketch, "E409", {"start": v(8.48, 32.08) * mm, "end": v(8.45, 31) * mm});
            skLineSegment(sketch, "E410", {"start": v(8.45, 31) * mm, "end": v(8.37, 29.56) * mm});
            skLineSegment(sketch, "E411", {"start": v(8.37, 29.56) * mm, "end": v(9.09, 28.3) * mm});
            skLineSegment(sketch, "E412", {"start": v(9.09, 28.3) * mm, "end": v(11.43, 28.3) * mm});
            skLineSegment(sketch, "E413", {"start": v(11.43, 28.3) * mm, "end": v(13.14, 30.31) * mm});
            skLineSegment(sketch, "E414", {"start": v(13.14, 30.31) * mm, "end": v(15.14, 32.26) * mm});
            skLineSegment(sketch, "E415", {"start": v(15.14, 32.26) * mm, "end": v(16.4, 34.67) * mm});
            skLineSegment(sketch, "E416", {"start": v(16.4, 34.67) * mm, "end": v(17.42, 37.72) * mm});
            skLineSegment(sketch, "E417", {"start": v(17.42, 37.72) * mm, "end": v(17.42, 41.36) * mm});
            skLineSegment(sketch, "E418", {"start": v(17.42, 41.36) * mm, "end": v(16.4, 42.84) * mm});
            skLineSegment(sketch, "E419", {"start": v(16.4, 42.84) * mm, "end": v(15.42, 43.52) * mm});
            skLineSegment(sketch, "E420", {"start": v(15.42, 43.52) * mm, "end": v(12.12, 43.52) * mm});
            skLineSegment(sketch, "E421", {"start": v(12.12, 43.52) * mm, "end": v(12.12, 42.9) * mm});
            skLineSegment(sketch, "E422", {"start": v(12.12, 42.9) * mm, "end": v(9.9, 42.9) * mm});
            skLineSegment(sketch, "E423", {"start": v(9.9, 42.9) * mm, "end": v(10.1, 42.33) * mm});
            skLineSegment(sketch, "E424", {"start": v(10.1, 42.33) * mm, "end": v(8.37, 42.33) * mm});
            skLineSegment(sketch, "E425", {"start": v(8.37, 42.33) * mm, "end": v(8.59, 41.65) * mm});
            skLineSegment(sketch, "E426", {"start": v(8.59, 41.65) * mm, "end": v(7.33, 41.65) * mm});
            skLineSegment(sketch, "E427", {"start": v(7.33, 41.65) * mm, "end": v(7.33, 41.15) * mm});
            skLineSegment(sketch, "E428", {"start": v(7.33, 41.15) * mm, "end": v(6.29, 41.15) * mm});
            skLineSegment(sketch, "E429", {"start": v(6.29, 41.15) * mm, "end": v(6.29, 40.6) * mm});
            skLineSegment(sketch, "E430", {"start": v(6.29, 40.6) * mm, "end": v(5.46, 40.6) * mm});
            skLineSegment(sketch, "E431", {"start": v(-3.53, 28.7) * mm, "end": v(-2.08, 33.01) * mm});
            skLineSegment(sketch, "E432", {"start": v(-2.08, 33.01) * mm, "end": v(0.59, 36.15) * mm});
            skLineSegment(sketch, "E433", {"start": v(0.59, 36.15) * mm, "end": v(4.42, 39.67) * mm});
            skLineSegment(sketch, "E434", {"start": v(4.42, 39.67) * mm, "end": v(5.46, 40.6) * mm});
            skLineSegment(sketch, "E435", {"start": v(69.2, -6.25) * mm, "end": v(66.4, -10.78) * mm});
            skLineSegment(sketch, "E436", {"start": v(66.4, -10.78) * mm, "end": v(65.39, -11.14) * mm});
            skLineSegment(sketch, "E437", {"start": v(65.39, -11.14) * mm, "end": v(65.95, -7.83) * mm});
            skLineSegment(sketch, "E438", {"start": v(65.95, -7.83) * mm, "end": v(67.93, -3.15) * mm});
            skLineSegment(sketch, "E439", {"start": v(67.93, -3.15) * mm, "end": v(72.81, 2.45) * mm});
            skLineSegment(sketch, "E440", {"start": v(72.81, 2.45) * mm, "end": v(73.23, 2.09) * mm});
            skLineSegment(sketch, "E441", {"start": v(73.23, 2.09) * mm, "end": v(72.66, -0.6) * mm});
            skLineSegment(sketch, "E442", {"start": v(72.66, -0.6) * mm, "end": v(71.34, -3) * mm});
            skLineSegment(sketch, "E443", {"start": v(71.34, -3) * mm, "end": v(69.2, -6.25) * mm});
            skLineSegment(sketch, "E444", {"start": v(-32.66, 34.48) * mm, "end": v(-32.66, 33.97) * mm});
            skLineSegment(sketch, "E445", {"start": v(64.9, 11.53) * mm, "end": v(67.8, 14.94) * mm});
            skLineSegment(sketch, "E446", {"start": v(67.8, 14.94) * mm, "end": v(68.1, 17.22) * mm});
            skLineSegment(sketch, "E447", {"start": v(68.1, 17.22) * mm, "end": v(67.14, 16.5) * mm});
            skLineSegment(sketch, "E448", {"start": v(67.14, 16.5) * mm, "end": v(66.17, 15.04) * mm});
            skLineSegment(sketch, "E449", {"start": v(66.17, 15.04) * mm, "end": v(64.12, 12.63) * mm});
            skLineSegment(sketch, "E450", {"start": v(64.12, 12.63) * mm, "end": v(64.41, 11.53) * mm});
            skLineSegment(sketch, "E451", {"start": v(64.41, 11.53) * mm, "end": v(64.9, 11.53) * mm});
            skLineSegment(sketch, "E452", {"start": v(-32.04, 15.59) * mm, "end": v(-32.87, 13.8) * mm});
            skLineSegment(sketch, "E453", {"start": v(-32.87, 13.8) * mm, "end": v(-32.87, 12.47) * mm});
            skLineSegment(sketch, "E454", {"start": v(-31, 16.96) * mm, "end": v(-30.67, 16.7) * mm});
            skLineSegment(sketch, "E455", {"start": v(-30.67, 16.7) * mm, "end": v(-30.67, 14.41) * mm});
            skLineSegment(sketch, "E456", {"start": v(-30.67, 14.41) * mm, "end": v(-31.8, 12.5) * mm});
            skLineSegment(sketch, "E457", {"start": v(-31.8, 12.5) * mm, "end": v(-31.8, 11.35) * mm});
            skLineSegment(sketch, "E458", {"start": v(-31.8, 11.35) * mm, "end": v(-32.83, 11.35) * mm});
            skLineSegment(sketch, "E459", {"start": v(-32.83, 11.35) * mm, "end": v(-32.87, 12.47) * mm});
            skLineSegment(sketch, "E460", {"start": v(-36.3, 7.8) * mm, "end": v(-34.5, 12.55) * mm});
            skLineSegment(sketch, "E461", {"start": v(-34.5, 12.55) * mm, "end": v(-34.06, 10.21) * mm});
            skLineSegment(sketch, "E462", {"start": v(-34.06, 10.21) * mm, "end": v(-33.27, 10.21) * mm});
            skLineSegment(sketch, "E463", {"start": v(-33.27, 10.21) * mm, "end": v(-33.18, 9.65) * mm});
            skLineSegment(sketch, "E464", {"start": v(-33.18, 9.65) * mm, "end": v(-33.18, 9.02) * mm});
            skLineSegment(sketch, "E465", {"start": v(-33.18, 9.02) * mm, "end": v(-33.53, 8.47) * mm});
            skLineSegment(sketch, "E466", {"start": v(-33.53, 8.47) * mm, "end": v(-34.03, 8.38) * mm});
            skLineSegment(sketch, "E467", {"start": v(-34.03, 8.38) * mm, "end": v(-34.3, 7.71) * mm});
            skLineSegment(sketch, "E468", {"start": v(-34.3, 7.71) * mm, "end": v(-34.57, 7.2) * mm});
            skLineSegment(sketch, "E469", {"start": v(-34.57, 7.2) * mm, "end": v(-34.87, 6.63) * mm});
            skLineSegment(sketch, "E470", {"start": v(-34.87, 6.63) * mm, "end": v(-35.27, 6.04) * mm});
            skLineSegment(sketch, "E471", {"start": v(-35.27, 6.04) * mm, "end": v(-35.27, 5.52) * mm});
            skLineSegment(sketch, "E472", {"start": v(-35.27, 5.52) * mm, "end": v(-35.85, 5.53) * mm});
            skLineSegment(sketch, "E473", {"start": v(-35.85, 5.53) * mm, "end": v(-35.85, 5) * mm});
            skLineSegment(sketch, "E474", {"start": v(-35.85, 5) * mm, "end": v(-36.44, 5) * mm});
            skLineSegment(sketch, "E475", {"start": v(-36.44, 5) * mm, "end": v(-36.42, 6.49) * mm});
            skLineSegment(sketch, "E476", {"start": v(-36.42, 6.49) * mm, "end": v(-36.3, 7.8) * mm});
            skSolve(sketch);
        }
        {
            var Q0;
            Q0=makeQuery(id+"F0.imprint","IMPRINT",FACE,{"disambiguationData":[TD([[makeQuery(id+"F0.imprint","IMPRINT",EDGE,{"derivedFrom":sQuery(id+"F0.wireOp",EDGE,"nEZZddXh-EgMC-Oc1K-fFZh-EI3aFNxccmXD")}),1.0]])]});
            var Q1;
            Q1=makeQuery(id+"F0.imprint","IMPRINT",FACE,{"disambiguationData":[TD([[makeQuery(id+"F0.imprint","IMPRINT",EDGE,{"derivedFrom":sQuery(id+"F0.wireOp",EDGE,"E0")}),1.0]])]});
            var Q2;
            Q2=makeQuery(id+"F0.imprint","IMPRINT",FACE,{"disambiguationData":[TD([[makeQuery(id+"F0.imprint","IMPRINT",EDGE,{"derivedFrom":sQuery(id+"F0.wireOp",EDGE,"E139")}),-1.0]])]});
            var Q3;
            Q3=makeQuery(id+"F0.imprint","IMPRINT",FACE,{"disambiguationData":[TD([[makeQuery(id+"F0.imprint","IMPRINT",EDGE,{"derivedFrom":sQuery(id+"F0.wireOp",EDGE,"E46")}),-1.0]])]});
            var Q4;
            Q4=makeQuery(id+"F0.imprint","IMPRINT",FACE,{"disambiguationData":[TD([[makeQuery(id+"F0.imprint","IMPRINT",EDGE,{"derivedFrom":sQuery(id+"F0.wireOp",EDGE,"E161")}),1.0]])]});
            var Q5;
            Q5=makeQuery(id+"F0.imprint","IMPRINT",FACE,{"disambiguationData":[TD([[makeQuery(id+"F0.imprint","IMPRINT",EDGE,{"derivedFrom":sQuery(id+"F0.wireOp",EDGE,"E180")}),-1.0]])]});
            var Q6;
            Q6=makeQuery(id+"F0.imprint","IMPRINT",FACE,{"disambiguationData":[TD([[makeQuery(id+"F0.imprint","IMPRINT",EDGE,{"derivedFrom":sQuery(id+"F0.wireOp",EDGE,"E129")}),1.0]])]});
            extrude(context, id + "F1", {"entities" : qUnion([Q0, Q1, Q2, Q3, Q4, Q5, Q6]), "depth" : 25.4 * mm, "offsetDistance" : 25.4 * mm});
        }
        {
            var Q0;
            Q0=qCreatedBy(makeId("Front.planeOp"),FACE);
            var sketch = newSketch(context, id + "F2", { "sketchPlane" : qUnion([Q0])});
            skLineSegment(sketch, "E477", {"start": v(87.49, 46.77) * mm, "end": v(87.49, -25.18) * mm});
            skLineSegment(sketch, "E478", {"start": v(87.49, -25.18) * mm, "end": v(-99.3, -25.18) * mm});
            skLineSegment(sketch, "E479", {"start": v(-99.3, -25.18) * mm, "end": v(-99.3, 46.77) * mm});
            skLineSegment(sketch, "E480", {"start": v(-99.3, 46.77) * mm, "end": v(87.49, 46.77) * mm});
            skSolve(sketch);
        }
        {
            var Q0;
            Q0=makeQuery(id+"F2.imprint","IMPRINT",FACE,{"disambiguationData":[TD([[makeQuery(id+"F2.imprint","IMPRINT",EDGE,{"derivedFrom":sQuery(id+"F2.wireOp",EDGE,"E477")}),-1.0]])]});
            extrude(context, id + "F3", {"entities" : qUnion([Q0]), "oppositeDirection" : true, "depth" : 5.08 * mm, "offsetDistance" : 25.4 * mm});
        }
        {
            var Q0;
            Q0=qCreatedBy(makeId("Right.planeOp"),FACE);
            var sketch = newSketch(context, id + "F4", { "sketchPlane" : qUnion([Q0])});
            skLineSegment(sketch, "E481", {"start": v(63.46, -25.18) * mm, "end": v(5.04, -25.18) * mm});
            skLineSegment(sketch, "E482", {"start": v(5.07, 46.78) * mm, "end": v(5.04, -25.18) * mm});
            skLineSegment(sketch, "E483", {"start": v(63.46, -25.18) * mm, "end": v(63.46, 46.78) * mm});
            skLineSegment(sketch, "E484", {"start": v(63.46, 46.78) * mm, "end": v(5.07, 46.78) * mm});
            skSolve(sketch);
        }
        {
            var Q0;
            Q0=makeQuery(id+"F4.imprint","IMPRINT",FACE,{"disambiguationData":[TD([[makeQuery(id+"F4.imprint","IMPRINT",EDGE,{"derivedFrom":sQuery(id+"F4.wireOp",EDGE,"E481")}),-1.0]])]});
            extrude(context, id + "F5", {"entities" : qUnion([Q0]), "operationType" : NewBodyOperationType.ADD, "depth" : 10.16 * mm, "offsetDistance" : 25.4 * mm});
        }
    });
